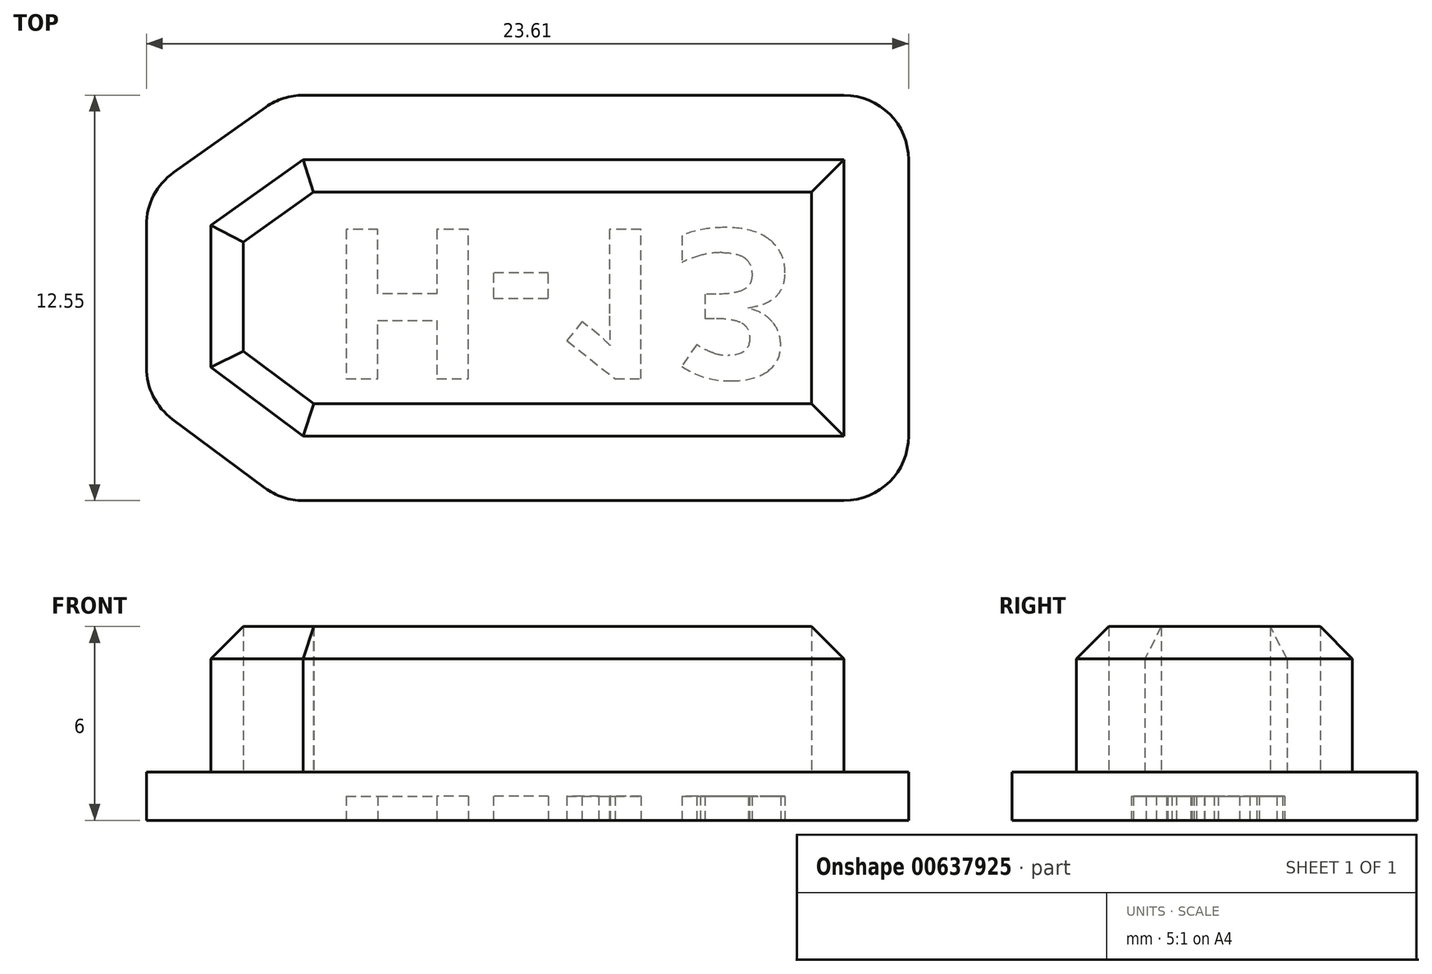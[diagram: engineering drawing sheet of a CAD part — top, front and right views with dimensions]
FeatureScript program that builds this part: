
annotation { "Feature Type Name" : "Feature", "Feature Type Description" : "" }
export const myFeature = defineFeature(function(context is Context, id is Id, definition is map)
    precondition{}
    {
        {
            var Q0;
            Q0=qCreatedBy(makeId("Top.planeOp"),FACE);
            var sketch = newSketch(context, id + "F0", { "sketchPlane" : qUnion([Q0])});
            skLineSegment(sketch, "E0", {"start": v(0, 0) * mm, "end": v(-16.75, 0) * mm});
            skLineSegment(sketch, "E1", {"start": v(0, 0) * mm, "end": v(0, -8.55) * mm});
            skLineSegment(sketch, "E2", {"start": v(0, -8.55) * mm, "end": v(-16.75, -8.55) * mm});
            skLineSegment(sketch, "E3", {"start": v(-19.6, -4.23) * mm, "end": v(-19.6, -2.02) * mm});
            skLineSegment(sketch, "E4", {"start": v(-19.6, -2.02) * mm, "end": v(-19.6, -6.43) * mm});
            skLineSegment(sketch, "E5", {"start": v(-19.6, -6.43) * mm, "end": v(-16.75, -8.55) * mm});
            skLineSegment(sketch, "E6", {"start": v(-19.6, -2.02) * mm, "end": v(-16.75, 0) * mm});
            skLineSegment(sketch, "E7.0", {"start": v(2, 2) * mm, "end": v(2, -10.55) * mm});
            skLineSegment(sketch, "E7.1", {"start": v(-21.6, -0.99) * mm, "end": v(-17.39, 2) * mm});
            skLineSegment(sketch, "E7.2", {"start": v(-21.6, -0.99) * mm, "end": v(-21.6, -7.43) * mm});
            skLineSegment(sketch, "E7.3", {"start": v(2, 2) * mm, "end": v(-17.39, 2) * mm});
            skLineSegment(sketch, "E7.4", {"start": v(-21.6, -7.43) * mm, "end": v(-17.41, -10.55) * mm});
            skLineSegment(sketch, "E7.5", {"start": v(2, -10.55) * mm, "end": v(-17.41, -10.55) * mm});
            skLineSegment(sketch, "E8.0", {"start": v(-1, -1) * mm, "end": v(-1, -7.55) * mm});
            skLineSegment(sketch, "E8.1", {"start": v(-18.6, -2.54) * mm, "end": v(-16.43, -1) * mm});
            skLineSegment(sketch, "E8.2", {"start": v(-18.6, -2.54) * mm, "end": v(-18.6, -5.92) * mm});
            skLineSegment(sketch, "E8.3", {"start": v(-1, -1) * mm, "end": v(-16.43, -1) * mm});
            skLineSegment(sketch, "E8.4", {"start": v(-18.6, -5.92) * mm, "end": v(-16.42, -7.55) * mm});
            skLineSegment(sketch, "E8.5", {"start": v(-1, -7.55) * mm, "end": v(-16.42, -7.55) * mm});
            skSolve(sketch);
        }
        {
            var Q0;
            Q0=makeQuery(id+"F0.imprint","IMPRINT",FACE,{"disambiguationData":[TD([[makeQuery(id+"F0.imprint","IMPRINT",EDGE,{"derivedFrom":sQuery(id+"F0.wireOp",EDGE,"E8.0")}),-1.0]])]});
            var Q1;
            Q1=makeQuery(id+"F0.imprint","IMPRINT",FACE,{"disambiguationData":[TD([[makeQuery(id+"F0.imprint","IMPRINT",EDGE,{"derivedFrom":sQuery(id+"F0.wireOp",EDGE,"E0")}),-1.0]])]});
            var Q2;
            Q2=makeQuery(id+"F0.imprint","IMPRINT",FACE,{"disambiguationData":[TD([[makeQuery(id+"F0.imprint","IMPRINT",EDGE,{"derivedFrom":sQuery(id+"F0.wireOp",EDGE,"E0")}),1.0]])]});
            extrude(context, id + "F1", {"entities" : qUnion([Q0, Q1, Q2]), "depth" : 1.5 * mm, "offsetDistance" : 25 * mm});
        }
        {
            var Q0;
            Q0=makeQuery(id+"F0.imprint","IMPRINT",FACE,{"disambiguationData":[TD([[makeQuery(id+"F0.imprint","IMPRINT",EDGE,{"derivedFrom":sQuery(id+"F0.wireOp",EDGE,"E0")}),1.0]])]});
            extrude(context, id + "F2", {"entities" : qUnion([Q0]), "operationType" : NewBodyOperationType.ADD, "depth" : 6 * mm, "offsetDistance" : 25 * mm});
        }
        {
            var Q0;
            Q0=makeQuery(id+"F1.opExtrude","CAP_FACE",FACE,{"disambiguationData":[OSD([sQuery(id+"F0.wireOp",EDGE,"E7.0"),sQuery(id+"F0.wireOp",EDGE,"E7.1"),sQuery(id+"F0.wireOp",EDGE,"E7.2"),sQuery(id+"F0.wireOp",EDGE,"E7.3"),sQuery(id+"F0.wireOp",EDGE,"E7.4"),sQuery(id+"F0.wireOp",EDGE,"E7.5")])],"isStart":true});
            var sketch = newSketch(context, id + "F3", { "sketchPlane" : qUnion([Q0])});
            skText(sketch, "E9", { "text": "H-13", "fontName": "OpenSans-Bold.ttf"});
            const initialGuessF3  = {"E9": [-0.016, 0.00216, 1, 0, 0.00466]};
            skSetInitialGuess(sketch, initialGuessF3);
            skSolve(sketch);
        }
        {
            var Q0;
            Q0 = qSketchRegion(id + "F3", true);
            extrude(context, id + "F4", {"entities" : qUnion([Q0]), "operationType" : NewBodyOperationType.REMOVE, "oppositeDirection" : true, "depth" : 0.75 * mm, "offsetDistance" : 25 * mm});
        }
        {
            var Q0;
            Q0=makeQuery(id+"F1.opExtrude","SWEPT_EDGE",EDGE,{"disambiguationData":[OSD([sQuery(id+"F0.wireOp",EDGE,"E7.0"),sQuery(id+"F0.wireOp",EDGE,"E7.3")])]});
            var Q1;
            Q1=makeQuery(id+"F1.opExtrude","SWEPT_EDGE",EDGE,{"disambiguationData":[OSD([sQuery(id+"F0.wireOp",EDGE,"E7.0"),sQuery(id+"F0.wireOp",EDGE,"E7.5")])]});
            var Q2;
            Q2=makeQuery(id+"F1.opExtrude","SWEPT_EDGE",EDGE,{"disambiguationData":[OSD([sQuery(id+"F0.wireOp",EDGE,"E7.1"),sQuery(id+"F0.wireOp",EDGE,"E7.2")])]});
            var Q3;
            Q3=makeQuery(id+"F1.opExtrude","SWEPT_EDGE",EDGE,{"disambiguationData":[OSD([sQuery(id+"F0.wireOp",EDGE,"E7.2"),sQuery(id+"F0.wireOp",EDGE,"E7.4")])]});
            var Q4;
            Q4=makeQuery(id+"F1.opExtrude","SWEPT_EDGE",EDGE,{"disambiguationData":[OSD([sQuery(id+"F0.wireOp",EDGE,"E7.1"),sQuery(id+"F0.wireOp",EDGE,"E7.3")])]});
            var Q5;
            Q5=makeQuery(id+"F1.opExtrude","SWEPT_EDGE",EDGE,{"disambiguationData":[OSD([sQuery(id+"F0.wireOp",EDGE,"E7.4"),sQuery(id+"F0.wireOp",EDGE,"E7.5")])]});
            fillet(context, id + "F5", {"entities" : qUnion([Q0, Q1, Q2, Q3, Q4, Q5]), "radius" : 2 * mm, "tangentPropagation" : true, "allowEdgeOverflow" : false});
        }
        {
            var Q0;
            Q0=makeQuery(id+"F2.opExtrude","CAP_EDGE",EDGE,{"disambiguationData":[OSD([sQuery(id+"F0.wireOp",EDGE,"E2")])],"isStart":false});
            var Q1;
            Q1=makeQuery(id+"F2.opExtrude","CAP_EDGE",EDGE,{"disambiguationData":[OSD([sQuery(id+"F0.wireOp",EDGE,"E1")])],"isStart":false});
            var Q2;
            Q2=makeQuery(id+"F2.opExtrude","CAP_EDGE",EDGE,{"disambiguationData":[OSD([sQuery(id+"F0.wireOp",EDGE,"E0")])],"isStart":false});
            var Q3;
            Q3=makeQuery(id+"F2.opExtrude","CAP_EDGE",EDGE,{"disambiguationData":[OSD([sQuery(id+"F0.wireOp",EDGE,"E6")])],"isStart":false});
            var Q4;
            Q4=makeQuery(id+"F2.opExtrude","CAP_EDGE",EDGE,{"disambiguationData":[OSD([sQuery(id+"F0.wireOp",EDGE,"E4")])],"isStart":false});
            var Q5;
            Q5=makeQuery(id+"F2.opExtrude","CAP_EDGE",EDGE,{"disambiguationData":[OSD([sQuery(id+"F0.wireOp",EDGE,"E5")])],"isStart":false});
            chamfer(context, id + "F6", {"entities" : qUnion([Q0, Q1, Q2, Q3, Q4, Q5]), "width" : 1 * mm, "tangentPropagation" : true});
        }
    });
